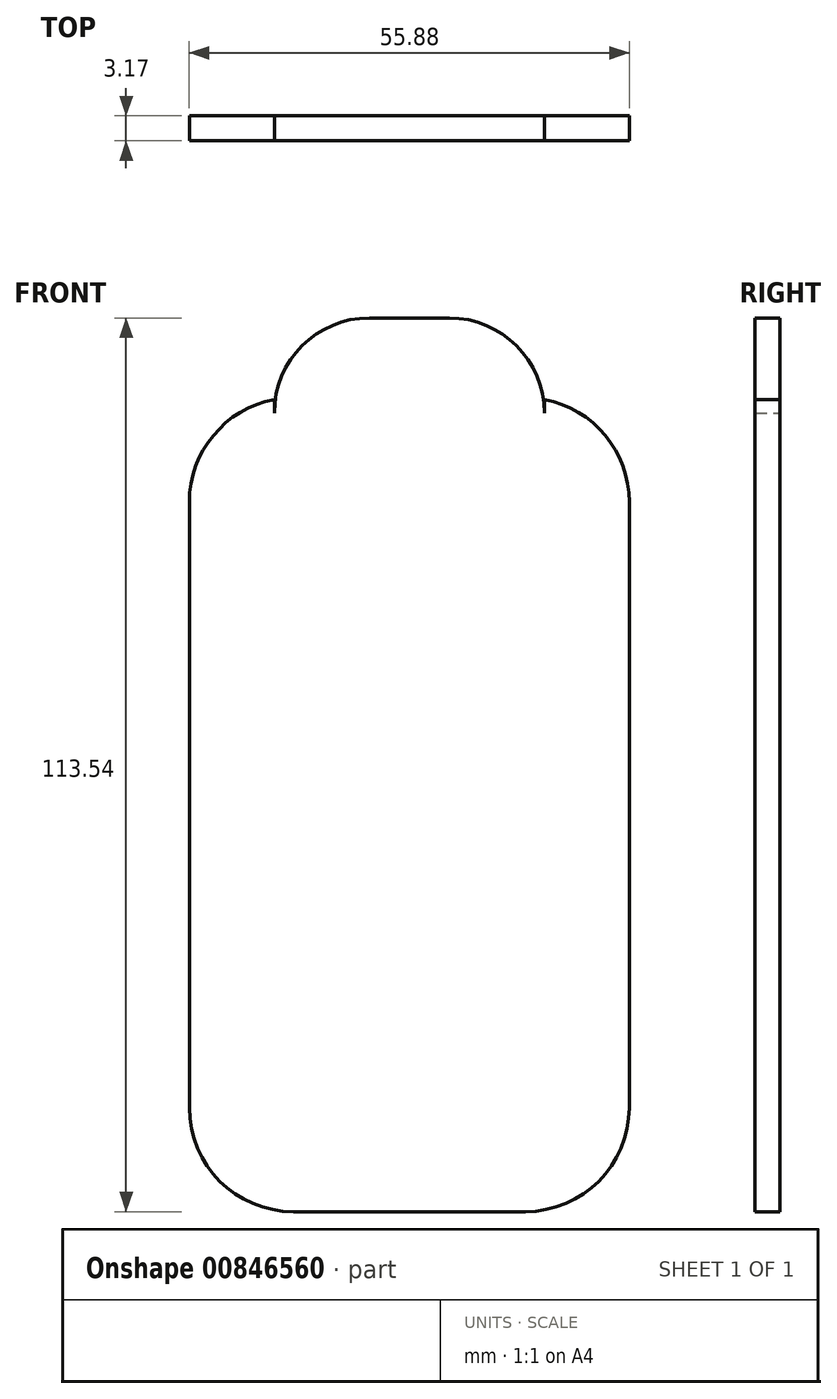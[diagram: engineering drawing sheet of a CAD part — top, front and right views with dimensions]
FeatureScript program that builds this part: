
annotation { "Feature Type Name" : "Feature", "Feature Type Description" : "" }
export const myFeature = defineFeature(function(context is Context, id is Id, definition is map)
    precondition{}
    {
        {
            var Q0;
            Q0=qCreatedBy(makeId("Front.planeOp"),FACE);
            var sketch = newSketch(context, id + "F0", { "sketchPlane" : qUnion([Q0])});
            skLineSegment(sketch, "E0.bottom", {"start": v(-24.53, 0) * mm, "end": v(4.94, 0) * mm});
            skLineSegment(sketch, "E0.top", {"start": v(-24.53, 103.38) * mm, "end": v(4.94, 103.38) * mm});
            skLineSegment(sketch, "E0.left", {"start": v(-37.74, 13.2) * mm, "end": v(-37.74, 90.17) * mm});
            skLineSegment(sketch, "E0.right", {"start": v(18.14, 13.2) * mm, "end": v(18.14, 90.17) * mm});
            skPoint(sketch, "E1.visualSharp", {"position": v(-37.74, 103.38) * mm});
            skArc(sketch, "E1.filletArc", {"start": v(-24.53, 103.38) * mm, "mid": v(-33.87, 99.5) * mm, "end": v(-37.74, 90.17) * mm});
            skPoint(sketch, "E2.visualSharp", {"position": v(18.14, 103.38) * mm});
            skArc(sketch, "E2.filletArc", {"start": v(18.14, 90.17) * mm, "mid": v(14.28, 99.5) * mm, "end": v(4.94, 103.38) * mm});
            skPoint(sketch, "E3.visualSharp", {"position": v(-37.74, 0) * mm});
            skArc(sketch, "E3.filletArc", {"start": v(-37.74, 13.2) * mm, "mid": v(-33.87, 3.87) * mm, "end": v(-24.53, 0) * mm});
            skPoint(sketch, "E4.visualSharp", {"position": v(18.14, 0) * mm});
            skArc(sketch, "E4.filletArc", {"start": v(4.94, 0) * mm, "mid": v(14.28, 3.87) * mm, "end": v(18.14, 13.2) * mm});
            skLineSegment(sketch, "E5.top", {"start": v(-14.88, 113.54) * mm, "end": v(-4.72, 113.54) * mm});
            skLineSegment(sketch, "E5.left", {"start": v(-26.94, 101.47) * mm, "end": v(-26.94, 103.16) * mm});
            skLineSegment(sketch, "E5.right", {"start": v(7.35, 101.47) * mm, "end": v(7.35, 103.16) * mm});
            skPoint(sketch, "E6.visualSharp", {"position": v(-26.94, 113.54) * mm});
            skArc(sketch, "E6.filletArc", {"start": v(-14.88, 113.54) * mm, "mid": v(-23.4, 110) * mm, "end": v(-26.94, 101.47) * mm});
            skPoint(sketch, "E7.visualSharp", {"position": v(7.35, 113.54) * mm});
            skArc(sketch, "E7.filletArc", {"start": v(7.35, 101.47) * mm, "mid": v(3.82, 110) * mm, "end": v(-4.72, 113.54) * mm});
            skSolve(sketch);
        }
        {
            var Q0;
            Q0=makeQuery(id+"F0.imprint","IMPRINT",FACE,{"disambiguationData":[TD([[makeQuery(id+"F0.imprint","IMPRINT",EDGE,{"derivedFrom":sQuery(id+"F0.wireOp",EDGE,"E0.bottom")}),1.0]])]});
            var Q1;
            {var subQ1=sQuery(id+"F0.wireOp",EDGE,"E0.top");Q1=makeQuery(id+"F0.imprint","IMPRINT",FACE,{"disambiguationData":[TD([[makeQuery(id+"F0.imprint","IMPRINT",EDGE,{"derivedFrom":subQ1}),1.0]])]});}
            extrude(context, id + "F1", {"entities" : qUnion([Q0, Q1]), "depth" : 3.17 * mm, "offsetDistance" : 25.4 * mm});
        }
    });
